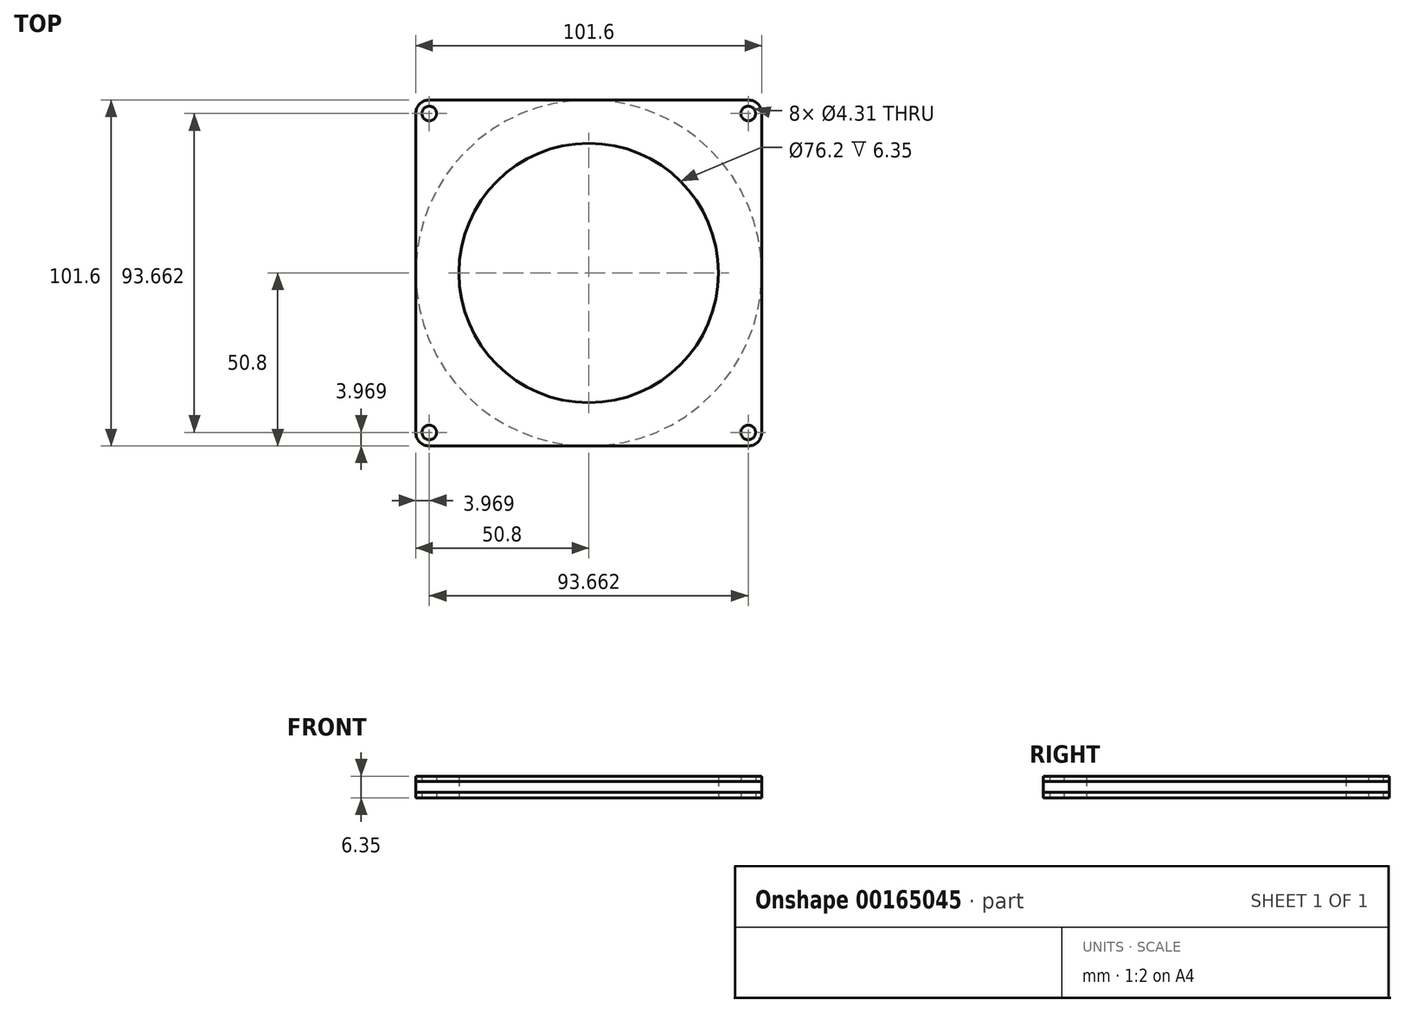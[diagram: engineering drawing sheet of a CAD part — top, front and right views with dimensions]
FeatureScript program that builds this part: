
annotation { "Feature Type Name" : "Feature", "Feature Type Description" : "" }
export const myFeature = defineFeature(function(context is Context, id is Id, definition is map)
    precondition{}
    {
        {
            var Q0;
            Q0=qCreatedBy(makeId("Top.planeOp"),FACE);
            var sketch = newSketch(context, id + "F0", { "sketchPlane" : qUnion([Q0])});
            skLineSegment(sketch, "E0.bottom", {"start": v(50.8, 50.8) * mm, "end": v(-50.8, 50.8) * mm});
            skLineSegment(sketch, "E0.top", {"start": v(50.8, -50.8) * mm, "end": v(-50.8, -50.8) * mm});
            skLineSegment(sketch, "E0.left", {"start": v(50.8, 50.8) * mm, "end": v(50.8, -50.8) * mm});
            skLineSegment(sketch, "E0.right", {"start": v(-50.8, 50.8) * mm, "end": v(-50.8, -50.8) * mm});
            skPoint(sketch, "E0.middle", {"position": v(0, 0) * mm});
            skLineSegment(sketch, "E1.bottom", {"start": v(-46.83, 46.83) * mm, "end": v(46.83, 46.83) * mm, "construction": true});
            skLineSegment(sketch, "E1.top", {"start": v(-46.83, -46.83) * mm, "end": v(46.83, -46.83) * mm, "construction": true});
            skLineSegment(sketch, "E1.left", {"start": v(-46.83, 46.83) * mm, "end": v(-46.83, -46.83) * mm, "construction": true});
            skLineSegment(sketch, "E1.right", {"start": v(46.83, 46.83) * mm, "end": v(46.83, -46.83) * mm, "construction": true});
            skLineSegment(sketch, "E2", {"start": v(0, 46.83) * mm, "end": v(0, 50.8) * mm, "construction": true});
            skCircle(sketch, "E3", {"center": v(-46.83, 46.83) * mm, "radius": 2.15 * mm});
            skCircle(sketch, "E4", {"center": v(46.83, 46.83) * mm, "radius": 2.15 * mm});
            skCircle(sketch, "E5", {"center": v(46.83, -46.83) * mm, "radius": 2.15 * mm});
            skCircle(sketch, "E6", {"center": v(-46.83, -46.83) * mm, "radius": 2.15 * mm});
            skCircle(sketch, "E7", {"center": v(0, 0) * mm, "radius": 38.1 * mm});
            skSolve(sketch);
        }
        {
            var Q0;
            Q0=qSketchRegion(id+"F0",true);
            extrude(context, id + "F1", {"entities" : qUnion([Q0]), "depth" : 1.59 * mm});
        }
        {
            var Q0;
            Q0=makeQuery(id+"F1.opExtrude","CAP_FACE",FACE,{"disambiguationData":[OSD([sQuery(id+"F0.wireOp",EDGE,"E0.bottom"),sQuery(id+"F0.wireOp",EDGE,"E0.top"),sQuery(id+"F0.wireOp",EDGE,"E0.left"),sQuery(id+"F0.wireOp",EDGE,"E0.right"),sQuery(id+"F0.wireOp",EDGE,"E3"),sQuery(id+"F0.wireOp",EDGE,"E4"),sQuery(id+"F0.wireOp",EDGE,"E5"),sQuery(id+"F0.wireOp",EDGE,"E6")])],"isStart":false});
            var sketch = newSketch(context, id + "F2", { "sketchPlane" : qUnion([Q0])});
            skCircle(sketch, "E8", {"center": v(0, 0) * mm, "radius": 50.8 * mm});
            skCircle(sketch, "E9", {"center": v(0, 0) * mm, "radius": 38.1 * mm});
            skSolve(sketch);
        }
        {
            var Q0;
            Q0=qSketchRegion(id+"F2",true);
            extrude(context, id + "F3", {"entities" : qUnion([Q0]), "operationType" : NewBodyOperationType.ADD, "depth" : 3.17 * mm});
        }
        {
            var Q0;
            Q0=makeQuery(id+"F3.opExtrude","CAP_FACE",FACE,{"disambiguationData":[OSD([sQuery(id+"F2.wireOp",EDGE,"E8")])],"isStart":false});
            var sketch = newSketch(context, id + "F4", { "sketchPlane" : qUnion([Q0])});
            skLineSegment(sketch, "E10.bottom", {"start": v(-50.8, -50.8) * mm, "end": v(50.8, -50.8) * mm});
            skLineSegment(sketch, "E10.top", {"start": v(-50.8, 50.8) * mm, "end": v(50.8, 50.8) * mm});
            skLineSegment(sketch, "E10.left", {"start": v(-50.8, -50.8) * mm, "end": v(-50.8, 50.8) * mm});
            skLineSegment(sketch, "E10.right", {"start": v(50.8, -50.8) * mm, "end": v(50.8, 50.8) * mm});
            skPoint(sketch, "E10.middle", {"position": v(0, 0) * mm});
            skLineSegment(sketch, "E11.bottom", {"start": v(-46.83, 46.83) * mm, "end": v(46.83, 46.83) * mm, "construction": true});
            skLineSegment(sketch, "E11.top", {"start": v(-46.83, -46.83) * mm, "end": v(46.83, -46.83) * mm, "construction": true});
            skLineSegment(sketch, "E11.left", {"start": v(-46.83, 46.83) * mm, "end": v(-46.83, -46.83) * mm, "construction": true});
            skLineSegment(sketch, "E11.right", {"start": v(46.83, 46.83) * mm, "end": v(46.83, -46.83) * mm, "construction": true});
            skCircle(sketch, "E12", {"center": v(-46.83, 46.83) * mm, "radius": 2.15 * mm});
            skCircle(sketch, "E13", {"center": v(46.83, -46.83) * mm, "radius": 2.15 * mm});
            skCircle(sketch, "E14", {"center": v(46.83, 46.83) * mm, "radius": 2.15 * mm});
            skCircle(sketch, "E15", {"center": v(-46.83, -46.83) * mm, "radius": 2.15 * mm});
            skCircle(sketch, "E16", {"center": v(0, 0) * mm, "radius": 38.1 * mm});
            skSolve(sketch);
        }
        {
            var Q0;
            Q0=qSketchRegion(id+"F4",true);
            extrude(context, id + "F5", {"entities" : qUnion([Q0]), "operationType" : NewBodyOperationType.ADD, "depth" : 1.59 * mm});
        }
        {
            var Q0;
            Q0=makeQuery(id+"F1.opExtrude","SWEPT_EDGE",EDGE,{"disambiguationData":[OSD([sQuery(id+"F0.wireOp",EDGE,"E0.bottom"),sQuery(id+"F0.wireOp",EDGE,"E0.right")])]});
            var Q1;
            Q1=makeQuery(id+"F1.opExtrude","SWEPT_EDGE",EDGE,{"disambiguationData":[OSD([sQuery(id+"F0.wireOp",EDGE,"E0.top"),sQuery(id+"F0.wireOp",EDGE,"E0.right")])]});
            var Q2;
            Q2=makeQuery(id+"F1.opExtrude","SWEPT_EDGE",EDGE,{"disambiguationData":[OSD([sQuery(id+"F0.wireOp",EDGE,"E0.top"),sQuery(id+"F0.wireOp",EDGE,"E0.left")])]});
            var Q3;
            Q3=makeQuery(id+"F1.opExtrude","SWEPT_EDGE",EDGE,{"disambiguationData":[OSD([sQuery(id+"F0.wireOp",EDGE,"E0.bottom"),sQuery(id+"F0.wireOp",EDGE,"E0.left")])]});
            var Q4;
            Q4=makeQuery(id+"F5.opExtrude","SWEPT_EDGE",EDGE,{"disambiguationData":[OSD([sQuery(id+"F4.wireOp",EDGE,"E10.top"),sQuery(id+"F4.wireOp",EDGE,"E10.left")])]});
            var Q5;
            Q5=makeQuery(id+"F5.opExtrude","SWEPT_EDGE",EDGE,{"disambiguationData":[OSD([sQuery(id+"F4.wireOp",EDGE,"E10.bottom"),sQuery(id+"F4.wireOp",EDGE,"E10.left")])]});
            var Q6;
            Q6=makeQuery(id+"F5.opExtrude","SWEPT_EDGE",EDGE,{"disambiguationData":[OSD([sQuery(id+"F4.wireOp",EDGE,"E10.bottom"),sQuery(id+"F4.wireOp",EDGE,"E10.right")])]});
            var Q7;
            Q7=makeQuery(id+"F5.opExtrude","SWEPT_EDGE",EDGE,{"disambiguationData":[OSD([sQuery(id+"F4.wireOp",EDGE,"E10.top"),sQuery(id+"F4.wireOp",EDGE,"E10.right")])]});
            fillet(context, id + "F6", {"entities" : qUnion([Q0, Q1, Q2, Q3, Q4, Q5, Q6, Q7]), "radius" : 3.97 * mm, "tangentPropagation" : true, "allowEdgeOverflow" : false});
        }
    });
